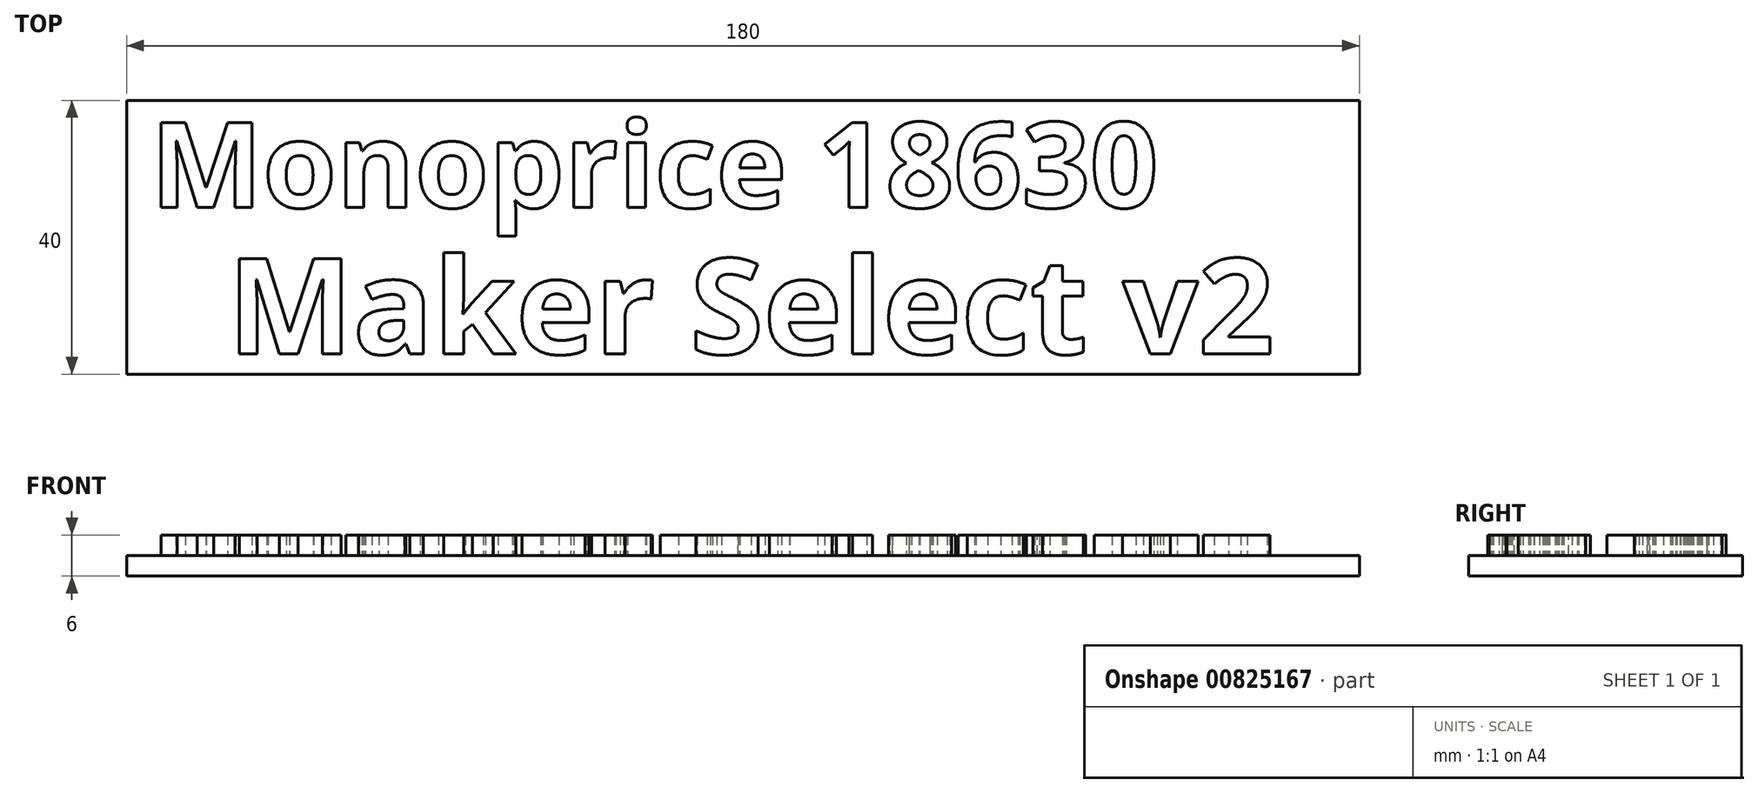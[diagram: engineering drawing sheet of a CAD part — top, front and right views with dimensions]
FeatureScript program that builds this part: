
annotation { "Feature Type Name" : "Feature", "Feature Type Description" : "" }
export const myFeature = defineFeature(function(context is Context, id is Id, definition is map)
    precondition{}
    {
        {
            var Q0;
            Q0=qCreatedBy(makeId("Top.planeOp"),FACE);
            var sketch = newSketch(context, id + "F0", { "sketchPlane" : qUnion([Q0])});
            skLineSegment(sketch, "E0.bottom", {"start": v(90, 20) * mm, "end": v(-90, 20) * mm});
            skLineSegment(sketch, "E0.top", {"start": v(90, -20) * mm, "end": v(-90, -20) * mm});
            skLineSegment(sketch, "E0.left", {"start": v(90, 20) * mm, "end": v(90, -20) * mm});
            skLineSegment(sketch, "E0.right", {"start": v(-90, 20) * mm, "end": v(-90, -20) * mm});
            skPoint(sketch, "E0.middle", {"position": v(0, 0) * mm});
            skSolve(sketch);
        }
        {
            var Q0;
            Q0 = qSketchRegion(id + "F0", true);
            extrude(context, id + "F1", {"entities" : qUnion([Q0]), "oppositeDirection" : true, "depth" : 3 * mm, "offsetDistance" : 25.4 * mm});
        }
        {
            var Q0;
            Q0=makeQuery(id+"F1.opExtrude","CAP_FACE",FACE,{"disambiguationData":[OSD([sQuery(id+"F0.wireOp",EDGE,"E0.bottom"),sQuery(id+"F0.wireOp",EDGE,"E0.top"),sQuery(id+"F0.wireOp",EDGE,"E0.left"),sQuery(id+"F0.wireOp",EDGE,"E0.right")])],"isStart":true});
            var sketch = newSketch(context, id + "F2", { "sketchPlane" : qUnion([Q0])});
            skText(sketch, "E1", { "text": "Monoprice 18630", "fontName": "OpenSans-Bold.ttf"});
            skText(sketch, "E2", { "text": "Maker Select v2", "fontName": "OpenSans-Bold.ttf"});
            const initialGuessF2  = {"E1": [-0.08655, 0.00433, 1, 0, 0.01254], "E2": [-0.0753, -0.01705, 1, 0, 0.01401]};
            skSetInitialGuess(sketch, initialGuessF2);
            skSolve(sketch);
        }
        {
            var Q0;
            Q0 = qSketchRegion(id + "F2", true);
            extrude(context, id + "F3", {"entities" : qUnion([Q0]), "operationType" : NewBodyOperationType.ADD, "depth" : 3 * mm, "offsetDistance" : 25.4 * mm});
        }
    });
